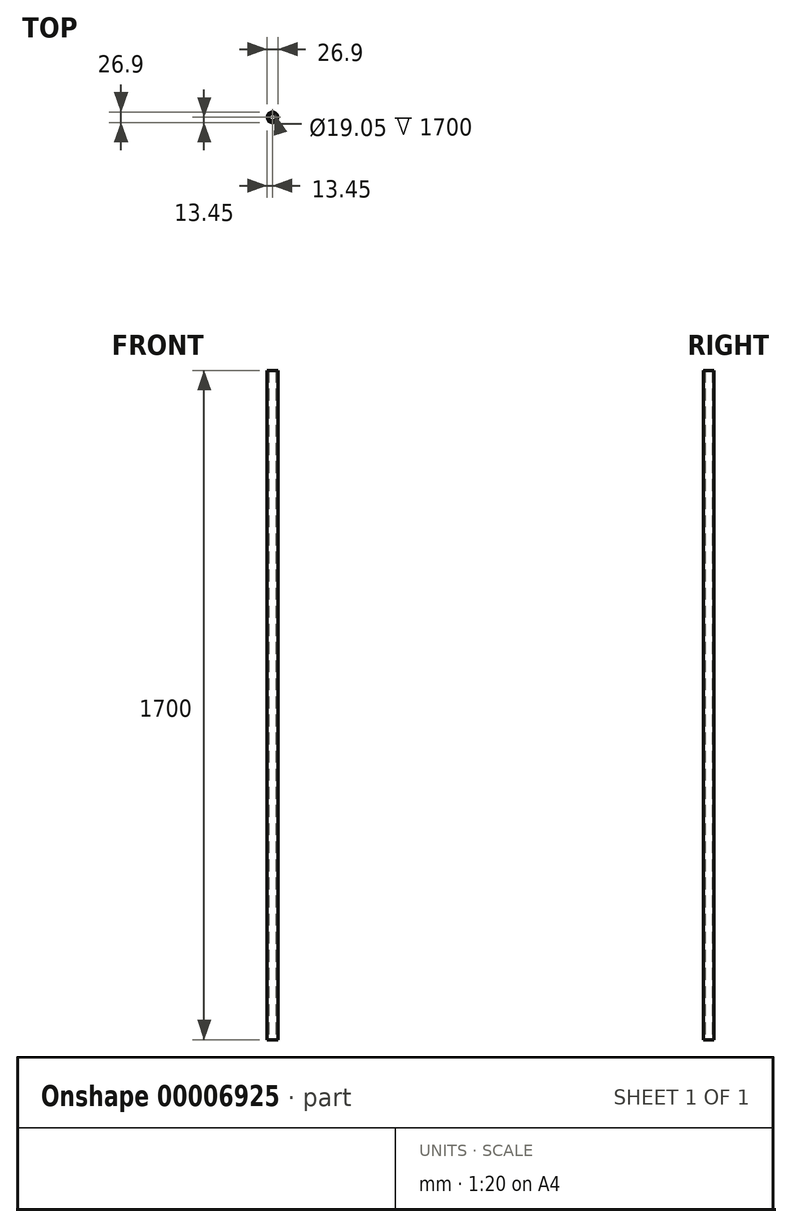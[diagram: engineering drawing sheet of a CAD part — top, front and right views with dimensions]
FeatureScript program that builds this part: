
annotation { "Feature Type Name" : "Feature", "Feature Type Description" : "" }
export const myFeature = defineFeature(function(context is Context, id is Id, definition is map)
    precondition{}
    {
        {
            var Q0;
            Q0=qCreatedBy(makeId("Top.planeOp"),FACE);
            var sketch = newSketch(context, id + "F0", { "sketchPlane" : qUnion([Q0])});
            skCircle(sketch, "E0", {"center": v(0, 0) * mm, "radius": 13.45 * mm});
            skCircle(sketch, "E1", {"center": v(0, 0) * mm, "radius": 9.53 * mm});
            skSolve(sketch);
        }
        {
            var Q0;
            Q0=qSketchRegion(id+"F0",true);
            extrude(context, id + "F1", {"entities" : qUnion([Q0]), "depth" : (1700) * mm});
        }
    });
